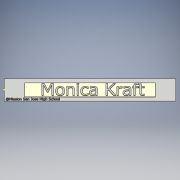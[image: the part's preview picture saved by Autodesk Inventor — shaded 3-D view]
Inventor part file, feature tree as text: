
AUTODESK INVENTOR PART (.ipt)
format: ipt  version: 2018 (Build 220112000, 112)  size: 2,179,584 bytes
history: native  units: in
note: dims shown in document units (in); Inventor stores cm internally (conversion verified against a paired STEP export)
features: sketch x8, extrude x7
ambient origin geometry x8: Origin, YZ Plane, XZ Plane, XY Plane, X Axis, Y Axis, Z Axis, Center Point
bodies: Solid1 (feature_tree)
feature tree (15):
  extrude  "Extrusion1"  Depth=0.009in TaperAngle=0.0deg
  extrude  "Extrusion2"  Depth=0.009in TaperAngle=0.0deg
  sketch  "Sketch3"  dims[d8=0.009in d9=0.0in d10=0.009in d11=0.0in]
  extrude  "Extrusion3"  Depth=0.009in TaperAngle=0.0deg
  extrude  "Extrusion4"  [1 undecoded]
  extrude  "Extrusion5"  [1 undecoded]
  sketch  "Sketch7"
  sketch  "Sketch8"
  extrude  "Extrusion6"  [1 undecoded]
  extrude  "Extrusion7"  [1 undecoded]
  sketch  "Sketch1"  dims[d0=3.0in d1=0.0in d2=0.009in d3=0.0in]
  sketch  "Sketch2"  dims[d4=0.01in d5=0.0in d6=0.009in d7=0.0in]
  sketch  "Sketch4"  dims[d12=0.009in d13=0.0in]
  sketch  "Sketch5"
  sketch  "Sketch6"
note: 4 required parameter values undecoded (feature->parameter linkage not recoverable at this tier; creation-order binding heuristic only, values carry confidence <= 0.55)
